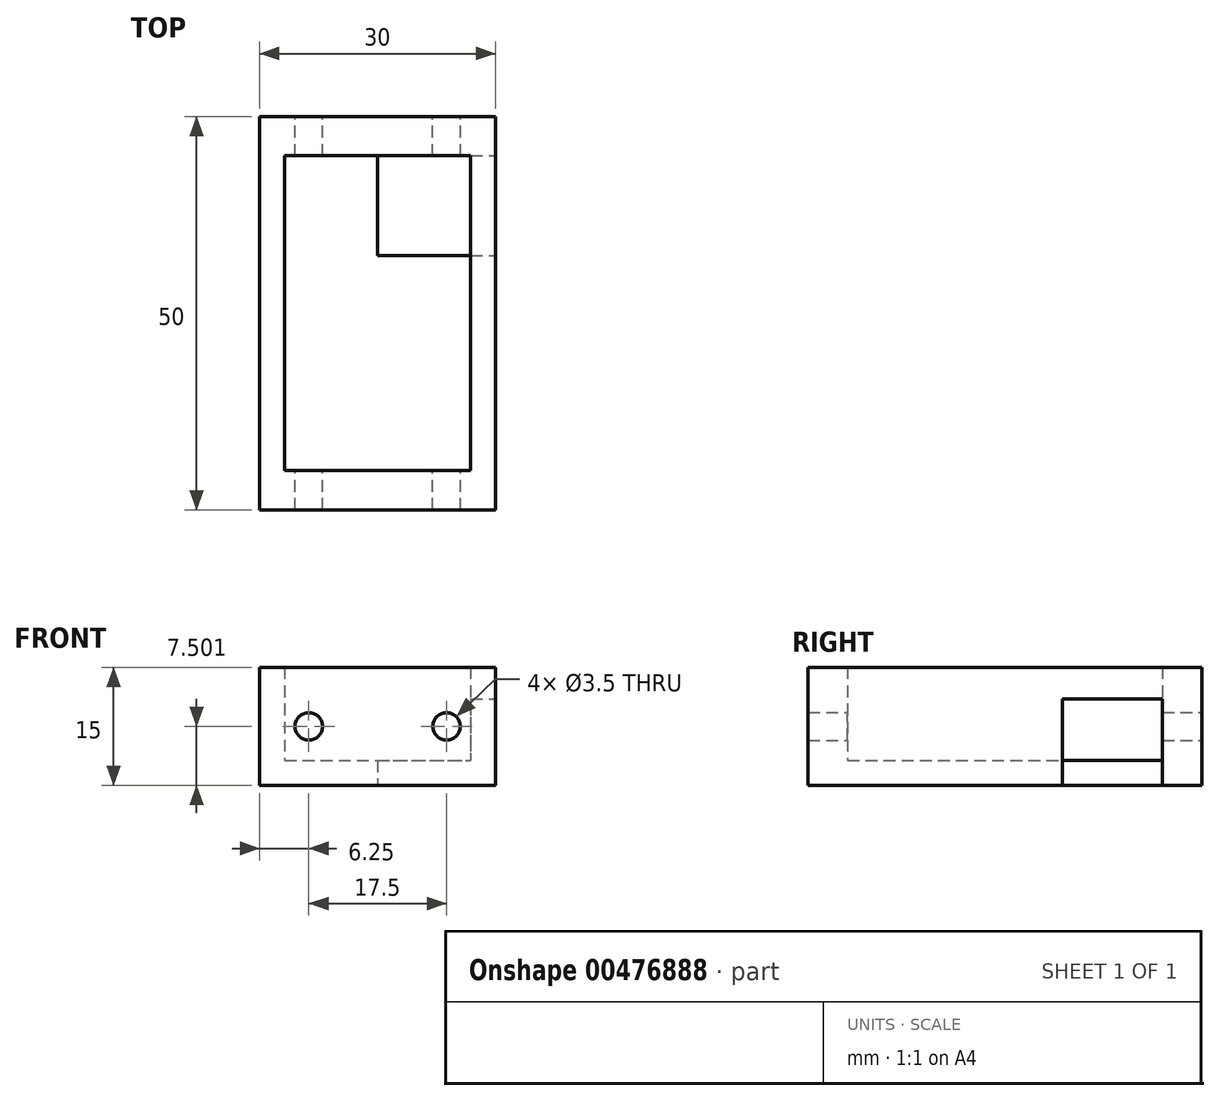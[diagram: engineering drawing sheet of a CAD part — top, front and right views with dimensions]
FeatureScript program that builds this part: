
annotation { "Feature Type Name" : "Feature", "Feature Type Description" : "" }
export const myFeature = defineFeature(function(context is Context, id is Id, definition is map)
    precondition{}
    {
        {
            var Q0;
            Q0=qCreatedBy(makeId("Front.planeOp"),FACE);
            var sketch = newSketch(context, id + "F0", { "sketchPlane" : qUnion([Q0])});
            skLineSegment(sketch, "E0.bottom", {"start": v(0, 0) * mm, "end": v(30, 0) * mm});
            skLineSegment(sketch, "E0.top", {"start": v(0, -15) * mm, "end": v(30, -15) * mm});
            skLineSegment(sketch, "E0.left", {"start": v(0, 0) * mm, "end": v(0, -15) * mm});
            skLineSegment(sketch, "E0.right", {"start": v(30, 0) * mm, "end": v(30, -15) * mm});
            skSolve(sketch);
        }
        {
            var Q0;
            Q0=makeQuery(id+"F0.imprint","IMPRINT",FACE,{"disambiguationData":[TD([[makeQuery(id+"F0.imprint","IMPRINT",EDGE,{"derivedFrom":sQuery(id+"F0.wireOp",EDGE,"E0.bottom")}),-1.0]])]});
            extrude(context, id + "F1", {"entities" : qUnion([Q0]), "depth" : 5 * mm});
        }
        {
            var Q0;
            Q0=makeQuery(id+"F1.opExtrude","CAP_FACE",FACE,{"disambiguationData":[OSD([sQuery(id+"F0.wireOp",EDGE,"E0.bottom"),sQuery(id+"F0.wireOp",EDGE,"E0.top"),sQuery(id+"F0.wireOp",EDGE,"E0.left"),sQuery(id+"F0.wireOp",EDGE,"E0.right")])],"isStart":false});
            var sketch = newSketch(context, id + "F2", { "sketchPlane" : qUnion([Q0])});
            skLineSegment(sketch, "E1.bottom", {"start": v(0, 0) * mm, "end": v(3.18, 0) * mm});
            skLineSegment(sketch, "E1.top", {"start": v(0, -15) * mm, "end": v(3.18, -15) * mm});
            skLineSegment(sketch, "E1.left", {"start": v(0, 0) * mm, "end": v(0, -15) * mm});
            skLineSegment(sketch, "E1.right", {"start": v(3.18, 0) * mm, "end": v(3.18, -15) * mm});
            skLineSegment(sketch, "E2.bottom", {"start": v(30, 0) * mm, "end": v(26.82, 0) * mm});
            skLineSegment(sketch, "E2.top", {"start": v(30, -15) * mm, "end": v(26.83, -15) * mm});
            skLineSegment(sketch, "E2.left", {"start": v(30, 0) * mm, "end": v(30, -15) * mm});
            skLineSegment(sketch, "E2.right", {"start": v(26.82, 0) * mm, "end": v(26.83, -15) * mm});
            skLineSegment(sketch, "E3.bottom", {"start": v(0, -11.82) * mm, "end": v(30, -11.82) * mm});
            skLineSegment(sketch, "E3.top", {"start": v(0, -15) * mm, "end": v(30, -15) * mm});
            skLineSegment(sketch, "E3.left", {"start": v(0, -11.82) * mm, "end": v(0, -15) * mm});
            skLineSegment(sketch, "E3.right", {"start": v(30, -11.82) * mm, "end": v(30, -15) * mm});
            skSolve(sketch);
        }
        {
            var Q0;
            Q0 = qSketchRegion(id + "F2", true);
            extrude(context, id + "F3", {"entities" : qUnion([Q0]), "operationType" : NewBodyOperationType.ADD, "depth" : 40 * mm});
        }
        {
            var Q0;
            Q0=makeQuery(id+"F3.opExtrude","CAP_FACE",FACE,{"disambiguationData":[OSD([sQuery(id+"F2.wireOp",EDGE,"E1.bottom"),sQuery(id+"F2.wireOp",EDGE,"E1.left"),sQuery(id+"F2.wireOp",EDGE,"E1.right"),sQuery(id+"F2.wireOp",EDGE,"E2.bottom"),sQuery(id+"F2.wireOp",EDGE,"E2.left"),sQuery(id+"F2.wireOp",EDGE,"E2.right"),sQuery(id+"F2.wireOp",EDGE,"E3.bottom"),sQuery(id+"F2.wireOp",EDGE,"E3.top"),sQuery(id+"F2.wireOp",EDGE,"E3.left"),sQuery(id+"F2.wireOp",EDGE,"E3.right")])],"isStart":false});
            var sketch = newSketch(context, id + "F4", { "sketchPlane" : qUnion([Q0])});
            skLineSegment(sketch, "E4.bottom", {"start": v(0, 0) * mm, "end": v(30, 0) * mm});
            skLineSegment(sketch, "E4.top", {"start": v(0, -15) * mm, "end": v(30, -15) * mm});
            skLineSegment(sketch, "E4.left", {"start": v(0, 0) * mm, "end": v(0, -15) * mm});
            skLineSegment(sketch, "E4.right", {"start": v(30, 0) * mm, "end": v(30, -15) * mm});
            skSolve(sketch);
        }
        {
            var Q0;
            Q0 = qSketchRegion(id + "F4", true);
            extrude(context, id + "F5", {"entities" : qUnion([Q0]), "operationType" : NewBodyOperationType.ADD, "depth" : 5 * mm});
        }
        {
            var Q0;
            Q0=makeQuery(id+"F1.opExtrude","CAP_FACE",FACE,{"disambiguationData":[OSD([sQuery(id+"F0.wireOp",EDGE,"E0.bottom"),sQuery(id+"F0.wireOp",EDGE,"E0.top"),sQuery(id+"F0.wireOp",EDGE,"E0.left"),sQuery(id+"F0.wireOp",EDGE,"E0.right")])],"isStart":true});
            var sketch = newSketch(context, id + "F6", { "sketchPlane" : qUnion([Q0])});
            skCircle(sketch, "E5", {"center": v(-23.75, -7.5) * mm, "radius": 1.75 * mm});
            skCircle(sketch, "E6", {"center": v(-6.25, -7.5) * mm, "radius": 1.75 * mm});
            skLineSegment(sketch, "E7", {"start": v(-23.75, -7.5) * mm, "end": v(-6.25, -7.5) * mm, "construction": true});
            skPoint(sketch, "E8", {"position": v(-15, -7.5) * mm});
            skSolve(sketch);
        }
        {
            var Q0;
            Q0 = qSketchRegion(id + "F6", true);
            extrude(context, id + "F7", {"entities" : qUnion([Q0]), "operationType" : NewBodyOperationType.REMOVE, "oppositeDirection" : true, "depth" : 112.27 * mm});
        }
        {
            var Q0;
            Q0=makeQuery(id+"F5.boolean.opBoolean","MERGE",FACE,{"derivedFrom":[makeQuery(id+"F3.boolean.opBoolean","MERGE",FACE,{"derivedFrom":[makeQuery(id+"F1.opExtrude","SWEPT_FACE",FACE,{"disambiguationData":[OSD([sQuery(id+"F0.wireOp",EDGE,"E0.right")])]}),makeQuery(id+"F3.opExtrude","SWEPT_FACE",FACE,{"disambiguationData":[OSD([sQuery(id+"F2.wireOp",EDGE,"E2.left"),sQuery(id+"F2.wireOp",EDGE,"E3.right")])]})]}),makeQuery(id+"F5.opExtrude","SWEPT_FACE",FACE,{"disambiguationData":[OSD([sQuery(id+"F4.wireOp",EDGE,"E4.right")])]})]});
            var sketch = newSketch(context, id + "F8", { "sketchPlane" : qUnion([Q0])});
            skLineSegment(sketch, "E9.bottom", {"start": v(-5, -4) * mm, "end": v(-17.68, -4) * mm});
            skLineSegment(sketch, "E9.top", {"start": v(-17.68, -15) * mm, "end": v(-5, -15) * mm});
            skLineSegment(sketch, "E9.left", {"start": v(-17.68, -4) * mm, "end": v(-17.68, -15) * mm});
            skLineSegment(sketch, "E9.right", {"start": v(-5, -4) * mm, "end": v(-5, -15) * mm});
            skSolve(sketch);
        }
        {
            var Q0;
            Q0 = qSketchRegion(id + "F8", true);
            extrude(context, id + "F9", {"entities" : qUnion([Q0]), "operationType" : NewBodyOperationType.REMOVE, "oppositeDirection" : true, "depth" : 15 * mm});
        }
    });
